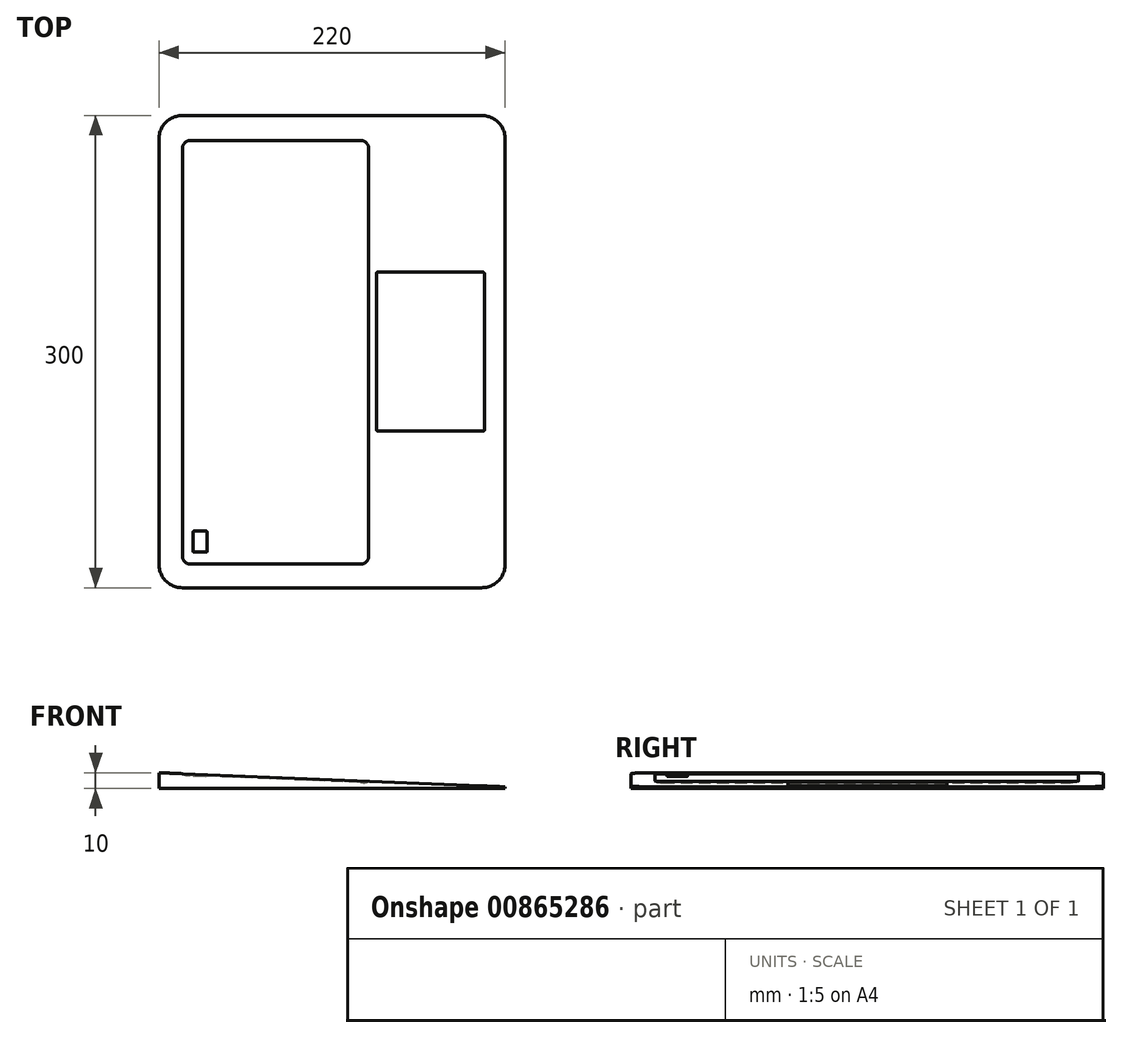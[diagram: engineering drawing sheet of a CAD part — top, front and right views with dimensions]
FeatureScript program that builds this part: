
annotation { "Feature Type Name" : "Feature", "Feature Type Description" : "" }
export const myFeature = defineFeature(function(context is Context, id is Id, definition is map)
    precondition{}
    {
        {
            var Q0;
            Q0=qCreatedBy(makeId("Front.planeOp"),FACE);
            var sketch = newSketch(context, id + "F0", { "sketchPlane" : qUnion([Q0])});
            skLineSegment(sketch, "E0", {"start": v(131.05, 0) * mm, "end": v(-88.95, 0) * mm});
            skLineSegment(sketch, "E1", {"start": v(-88.95, 0) * mm, "end": v(-88.95, 10) * mm});
            skLineSegment(sketch, "E2", {"start": v(131.05, 0) * mm, "end": v(131.05, 1) * mm});
            skLineSegment(sketch, "E3", {"start": v(131.05, 1) * mm, "end": v(-88.95, 10) * mm});
            skSolve(sketch);
        }
        {
            var Q0;
            Q0=makeQuery(id+"F0.imprint","IMPRINT",FACE,{"disambiguationData":[TD([[makeQuery(id+"F0.imprint","IMPRINT",EDGE,{"derivedFrom":sQuery(id+"F0.wireOp",EDGE,"E0")}),-1.0]])]});
            extrude(context, id + "F1", {"entities" : qUnion([Q0]), "depth" : 300 * mm, "offsetDistance" : 25 * mm});
        }
        {
            var Q0;
            Q0=makeQuery(id+"F1.opExtrude","CAP_EDGE",EDGE,{"disambiguationData":[OSD([sQuery(id+"F0.wireOp",EDGE,"E1")])],"isStart":false});
            var Q1;
            Q1=makeQuery(id+"F1.opExtrude","CAP_EDGE",EDGE,{"disambiguationData":[OSD([sQuery(id+"F0.wireOp",EDGE,"E2")])],"isStart":false});
            var Q2;
            Q2=makeQuery(id+"F1.opExtrude","CAP_EDGE",EDGE,{"disambiguationData":[OSD([sQuery(id+"F0.wireOp",EDGE,"E2")])],"isStart":true});
            var Q3;
            Q3=makeQuery(id+"F1.opExtrude","CAP_EDGE",EDGE,{"disambiguationData":[OSD([sQuery(id+"F0.wireOp",EDGE,"E1")])],"isStart":true});
            fillet(context, id + "F2", {"entities" : qUnion([Q0, Q1, Q2, Q3]), "radius" : 15 * mm, "tangentPropagation" : true, "allowEdgeOverflow" : false});
        }
        {
            var Q0;
            Q0=makeQuery(id+"F1.opExtrude","SWEPT_FACE",FACE,{"disambiguationData":[OSD([sQuery(id+"F0.wireOp",EDGE,"E3")])]});
            var sketch = newSketch(context, id + "F3", { "sketchPlane" : qUnion([Q0])});
            skLineSegment(sketch, "E4.bottom", {"start": v(-69.27, -285) * mm, "end": v(39.08, -285) * mm});
            skLineSegment(sketch, "E4.top", {"start": v(-69.27, -15.94) * mm, "end": v(39.08, -15.94) * mm});
            skLineSegment(sketch, "E4.left", {"start": v(-74.27, -280) * mm, "end": v(-74.27, -20.94) * mm});
            skLineSegment(sketch, "E4.right", {"start": v(44.08, -280) * mm, "end": v(44.08, -20.94) * mm});
            skPoint(sketch, "E5.visualSharp", {"position": v(-74.27, -285) * mm});
            skArc(sketch, "E5.filletArc", {"start": v(-74.27, -280) * mm, "mid": v(-72.8, -283.54) * mm, "end": v(-69.27, -285) * mm});
            skPoint(sketch, "E6.visualSharp", {"position": v(-74.27, -15.94) * mm});
            skArc(sketch, "E6.filletArc", {"start": v(-69.27, -15.94) * mm, "mid": v(-72.8, -17.4) * mm, "end": v(-74.27, -20.94) * mm});
            skPoint(sketch, "E7.visualSharp", {"position": v(44.08, -15.94) * mm});
            skArc(sketch, "E7.filletArc", {"start": v(44.08, -20.94) * mm, "mid": v(42.61, -17.4) * mm, "end": v(39.08, -15.94) * mm});
            skPoint(sketch, "E8.visualSharp", {"position": v(44.08, -285) * mm});
            skArc(sketch, "E8.filletArc", {"start": v(39.08, -285) * mm, "mid": v(42.61, -283.54) * mm, "end": v(44.08, -280) * mm});
            skSolve(sketch);
        }
        {
            var Q0;
            Q0=makeQuery(id+"F3.imprint","IMPRINT",FACE,{"disambiguationData":[TD([[makeQuery(id+"F3.imprint","IMPRINT",EDGE,{"derivedFrom":sQuery(id+"F3.wireOp",EDGE,"E4.bottom")}),1.0]])]});
            extrude(context, id + "F4", {"entities" : qUnion([Q0]), "operationType" : NewBodyOperationType.REMOVE, "oppositeDirection" : true, "depth" : 1 * mm, "offsetDistance" : 25 * mm});
        }
        {
            var Q0;
            Q0=makeQuery(id+"F4.boolean.opBoolean","COPY",FACE,{"derivedFrom":makeQuery(id+"F4.opExtrude","CAP_FACE",FACE,{"disambiguationData":[OSD([sQuery(id+"F3.wireOp",EDGE,"E4.bottom"),sQuery(id+"F3.wireOp",EDGE,"E4.top"),sQuery(id+"F3.wireOp",EDGE,"E4.left"),sQuery(id+"F3.wireOp",EDGE,"E4.right"),sQuery(id+"F3.wireOp",EDGE,"E5.filletArc"),sQuery(id+"F3.wireOp",EDGE,"E6.filletArc"),sQuery(id+"F3.wireOp",EDGE,"E7.filletArc"),sQuery(id+"F3.wireOp",EDGE,"E8.filletArc")])],"isStart":false})});
            fillet(context, id + "F5", {"entities" : qUnion([Q0]), "radius" : 5 * mm, "tangentPropagation" : true, "allowEdgeOverflow" : false});
        }
        {
            var Q0;
            Q0=makeQuery(id+"F1.opExtrude","SWEPT_FACE",FACE,{"disambiguationData":[OSD([sQuery(id+"F0.wireOp",EDGE,"E3")])]});
            var sketch = newSketch(context, id + "F6", { "sketchPlane" : qUnion([Q0])});
            skLineSegment(sketch, "E9.bottom", {"start": v(116.75, -99.55) * mm, "end": v(49.98, -99.55) * mm});
            skLineSegment(sketch, "E9.top", {"start": v(116.75, -200.45) * mm, "end": v(49.98, -200.45) * mm});
            skLineSegment(sketch, "E9.left", {"start": v(117.75, -100.55) * mm, "end": v(117.75, -199.45) * mm});
            skLineSegment(sketch, "E9.right", {"start": v(48.98, -100.55) * mm, "end": v(48.98, -199.45) * mm});
            skPoint(sketch, "E9.middle", {"position": v(83.37, -150) * mm});
            skPoint(sketch, "E9.middle.positionSnap0", {"position": v(130.9, -150) * mm});
            skPoint(sketch, "E9.centerSnap0", {"position": v(130.9, -150) * mm});
            skPoint(sketch, "E10.visualSharp", {"position": v(48.98, -200.45) * mm});
            skArc(sketch, "E10.filletArc", {"start": v(48.98, -199.45) * mm, "mid": v(49.27, -200.16) * mm, "end": v(49.98, -200.45) * mm});
            skPoint(sketch, "E11.visualSharp", {"position": v(48.98, -99.55) * mm});
            skArc(sketch, "E11.filletArc", {"start": v(49.98, -99.55) * mm, "mid": v(49.27, -99.84) * mm, "end": v(48.98, -100.55) * mm});
            skPoint(sketch, "E12.visualSharp", {"position": v(117.75, -99.55) * mm});
            skArc(sketch, "E12.filletArc", {"start": v(117.75, -100.55) * mm, "mid": v(117.46, -99.84) * mm, "end": v(116.75, -99.55) * mm});
            skPoint(sketch, "E13.visualSharp", {"position": v(117.75, -200.45) * mm});
            skArc(sketch, "E13.filletArc", {"start": v(116.75, -200.45) * mm, "mid": v(117.46, -200.16) * mm, "end": v(117.75, -199.45) * mm});
            skSolve(sketch);
        }
        {
            var Q0;
            Q0=makeQuery(id+"F6.imprint","IMPRINT",FACE,{"disambiguationData":[TD([[makeQuery(id+"F6.imprint","IMPRINT",EDGE,{"derivedFrom":sQuery(id+"F6.wireOp",EDGE,"E9.bottom")}),1.0]])]});
            extrude(context, id + "F7", {"entities" : qUnion([Q0]), "operationType" : NewBodyOperationType.REMOVE, "oppositeDirection" : true, "depth" : 0.1 * mm, "offsetDistance" : 25 * mm});
        }
        {
            var Q0;
            Q0=makeQuery(id+"F4.boolean.opBoolean","COPY",FACE,{"derivedFrom":makeQuery(id+"F4.opExtrude","CAP_FACE",FACE,{"disambiguationData":[OSD([sQuery(id+"F3.wireOp",EDGE,"E4.bottom"),sQuery(id+"F3.wireOp",EDGE,"E4.top"),sQuery(id+"F3.wireOp",EDGE,"E4.left"),sQuery(id+"F3.wireOp",EDGE,"E4.right"),sQuery(id+"F3.wireOp",EDGE,"E5.filletArc"),sQuery(id+"F3.wireOp",EDGE,"E6.filletArc"),sQuery(id+"F3.wireOp",EDGE,"E7.filletArc"),sQuery(id+"F3.wireOp",EDGE,"E8.filletArc")])],"isStart":false})});
            var sketch = newSketch(context, id + "F8", { "sketchPlane" : qUnion([Q0])});
            skLineSegment(sketch, "E14.bottom", {"start": v(-67.05, -277.29) * mm, "end": v(-59.07, -277.29) * mm});
            skLineSegment(sketch, "E14.top", {"start": v(-67.05, -264.1) * mm, "end": v(-59.07, -264.1) * mm});
            skLineSegment(sketch, "E14.left", {"start": v(-67.55, -276.79) * mm, "end": v(-67.55, -264.6) * mm});
            skLineSegment(sketch, "E14.right", {"start": v(-58.57, -276.79) * mm, "end": v(-58.57, -264.6) * mm});
            skPoint(sketch, "E15.visualSharp", {"position": v(-67.55, -277.29) * mm});
            skArc(sketch, "E15.filletArc", {"start": v(-67.55, -276.79) * mm, "mid": v(-67.4, -277.14) * mm, "end": v(-67.05, -277.29) * mm});
            skPoint(sketch, "E16.visualSharp", {"position": v(-67.55, -264.1) * mm});
            skArc(sketch, "E16.filletArc", {"start": v(-67.05, -264.1) * mm, "mid": v(-67.4, -264.24) * mm, "end": v(-67.55, -264.6) * mm});
            skPoint(sketch, "E17.visualSharp", {"position": v(-58.57, -264.1) * mm});
            skArc(sketch, "E17.filletArc", {"start": v(-58.57, -264.6) * mm, "mid": v(-58.71, -264.24) * mm, "end": v(-59.07, -264.1) * mm});
            skPoint(sketch, "E18.visualSharp", {"position": v(-58.57, -277.29) * mm});
            skArc(sketch, "E18.filletArc", {"start": v(-59.07, -277.29) * mm, "mid": v(-58.71, -277.14) * mm, "end": v(-58.57, -276.79) * mm});
            skSolve(sketch);
        }
        {
            var Q0;
            Q0=makeQuery(id+"F8.imprint","IMPRINT",FACE,{"disambiguationData":[TD([[makeQuery(id+"F8.imprint","IMPRINT",EDGE,{"derivedFrom":sQuery(id+"F8.wireOp",EDGE,"E14.bottom")}),1.0]])]});
            extrude(context, id + "F9", {"entities" : qUnion([Q0]), "operationType" : NewBodyOperationType.ADD, "depth" : 1 * mm, "offsetDistance" : 25 * mm});
        }
    });
